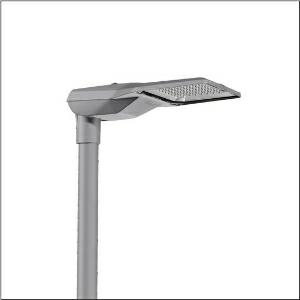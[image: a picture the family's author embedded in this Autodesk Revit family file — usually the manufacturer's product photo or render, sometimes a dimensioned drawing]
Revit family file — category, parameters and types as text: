
# Revit family: streetlight_sl_21_midi___st1_5a_5xe3p43s08lb_fbc0
name_source: partatom
category: Lighting Fixtures
units: mm (PartAtom-declared; Revit-internal decimal feet)

## family parameters
Cut with Voids When Loaded = No
Host = Face
Light Source = No
Part Type = Normal
Room Calculation Point = No
Round Connector Dimension = Use Diameter
Shared = No

## types (1)
- --- (1 x LED, 14690 lm, 99.6 W, 4000K)
    Apparent Load = 100 VA
    CIE Flux Codes = 22 53 95 100 100
    Color Rendering = 70
    Color Temperature = 4000K
    Default Elevation = 1800 mm
    Description = Streetlight SL 21 midi, mast luminaire, primary light control with lens, of PMMA, primary optical cover: cover, of toughened safety glass, transparent, light distribution: ST1.5a, light emission: direct distribution, primary light characteristic: asymmetric, installation type: side-entry, post-top, LED, High Power LED, rated luminous flux: 14.690lm, luminous efficacy: 148lm/W, light colour: 740, colour temperature: 4000K, control gear: D4i, control: overheat protection, constant luminous flux control, time-dependent luminous flux control, flexible luminous flux parameterisation, pre-setting: logarithmic dimming characteristic, mains connection: 230..240V, AC, 50/60Hz, start of lifetime: 100W, end of service life: 102W, reduction: 46W, luminaire housing, of diecast aluminium, powder-coated, Siteco® metallic grey (DB 702S), corrosivity category C5 mid according to DIN EN ISO 12944, please order mast flange separately, inclination adjustable: 0°, 5°, 10°, 15°, sealing non-destructively replaceable, multi-level sealing system, length: 644mm, width: 335mm, height: 110mm, mast flange for spigot size: 42mm (side-entry): 5XC10008XM4, 60/48mm (side-entry/post-top): 5XC10108XM2, 76/60mm (side-entry/post-top): 5XC10108XM1, mounting height: 4..8m, Smart Interface above, protection rating (complete): IP66, insulation class (complete): insulation class II (safety insulation), certification: CE, ENEC, ENEC+, VDE, impact resistance: IK10, permissible operating ambient temperature for outdoor applications: -40..+50°C, standard-compliant lighting for roads and squares, packaging unit: 1 piece

Light Distribution: ST1.5a
    Height = 111 mm
    Lamp = 1 x LED
    Lamp Light Flux = 14690 lm
    Lamp Power = 99.6 W
    Lamp count = 1
    Length = 644 mm
    Luminous efficacy = 147 lm/W
    Manufacturer = Siteco
    ModVariant = No
    Model = 5XE3P43S08LB
    Number of Poles = 1
    OnlyDefault = Yes
    Power Factor = 1
    Product Name = Streetlight SL 21 midi | ST1.5a
    Product group = mast luminaire | pylon top
    ProductGroupID = 6100
    Protection Class = Protection class II
    Protection Degree = IP 66
    RLX_Detail_Level = 1
    RLX_Emergency_Light_Flux = 0 lm
    RLX_Emergency_Type = 0
    RLX_Emergency_Type_DB = No
    RlxData = <blob elided: 30317 chars, md5=bc4216c5>
    Socket = socket
    Standby Power = 0 W
    System Light Flux = 14690 lm
    System Power = 100 W
    Type Comments = factory setting: luminous flux: 100 % | dim-lin: 254 | 1020 mA
    Type Image = l_1004302.jpg
    URL = http://relux.com
    VarID = @adj_032695
    Voltage = 0 V
    Weight = 0.00 kg
    Width = 336 mm

## geometry (parser evidence)
native form markers: Blend x4, Sweep x12
no freeform markers — native parametric forms only
